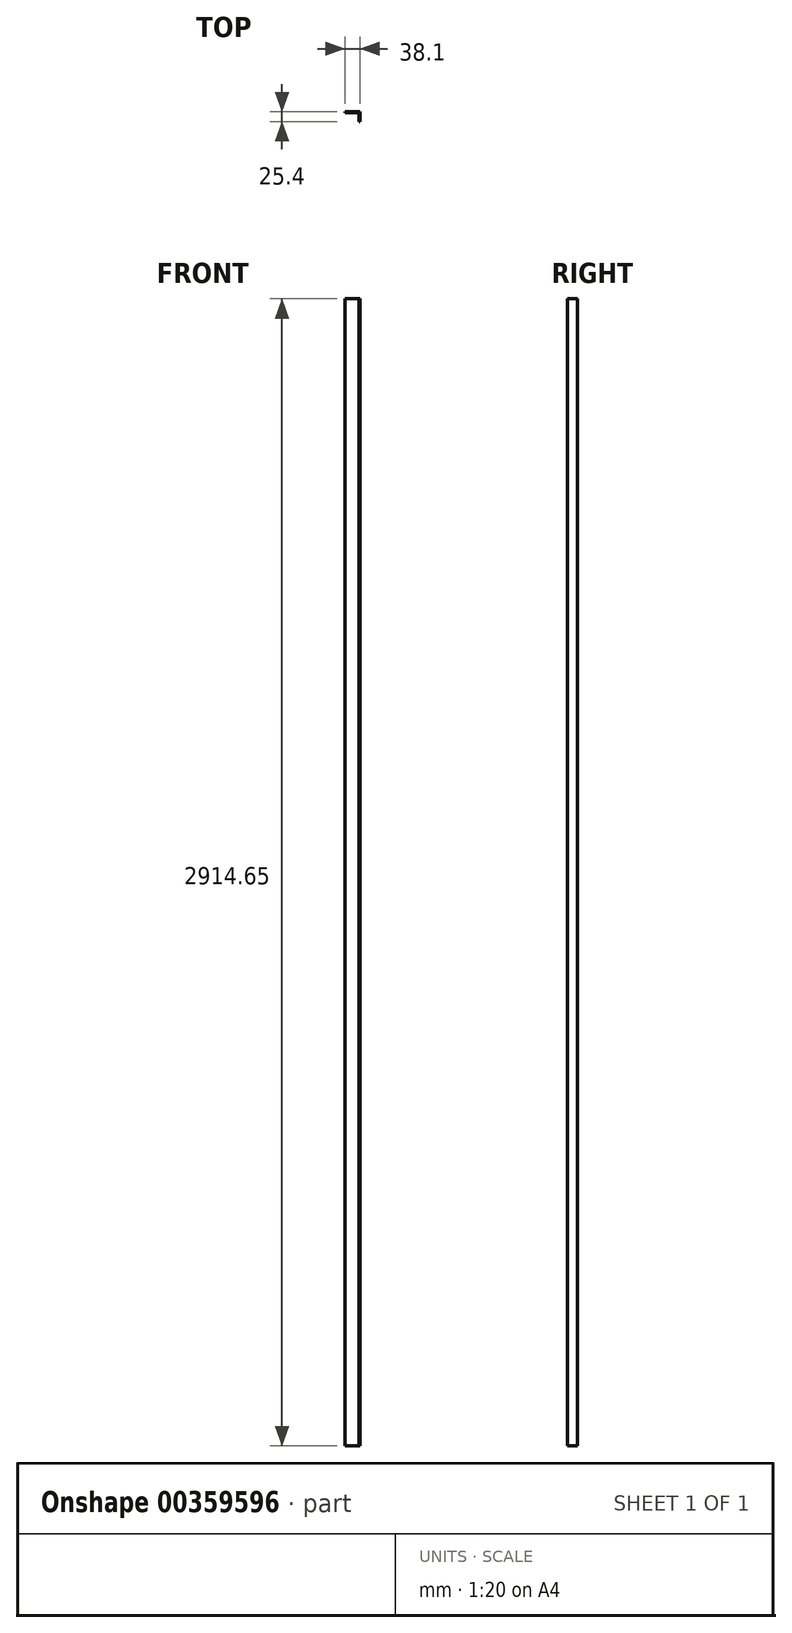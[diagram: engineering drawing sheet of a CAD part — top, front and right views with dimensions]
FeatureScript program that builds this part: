
annotation { "Feature Type Name" : "Feature", "Feature Type Description" : "" }
export const myFeature = defineFeature(function(context is Context, id is Id, definition is map)
    precondition{}
    {
        {
            var Q0;
            Q0=qCreatedBy(makeId("Top.planeOp"),FACE);
            var sketch = newSketch(context, id + "F0", { "sketchPlane" : qUnion([Q0])});
            skLineSegment(sketch, "E0", {"start": v(0, 0) * mm, "end": v(34.93, 0) * mm});
            skLineSegment(sketch, "E1", {"start": v(34.93, 0) * mm, "end": v(34.93, -22.22) * mm});
            skLineSegment(sketch, "E2", {"start": v(34.93, -22.22) * mm, "end": v(38.1, -22.22) * mm});
            skLineSegment(sketch, "E3", {"start": v(38.1, -22.22) * mm, "end": v(38.1, 3.18) * mm});
            skLineSegment(sketch, "E4", {"start": v(38.1, 3.18) * mm, "end": v(0, 3.18) * mm});
            skLineSegment(sketch, "E5", {"start": v(0, 3.18) * mm, "end": v(0, 0) * mm});
            skSolve(sketch);
        }
        {
            var Q0;
            Q0=makeQuery(id+"F0.imprint","IMPRINT",FACE,{"disambiguationData":[TD([[makeQuery(id+"F0.imprint","IMPRINT",EDGE,{"derivedFrom":sQuery(id+"F0.wireOp",EDGE,"E0")}),1.0]])]});
            extrude(context, id + "F1", {"entities" : qUnion([Q0]), "depth" : 2914.65 * mm});
        }
    });
